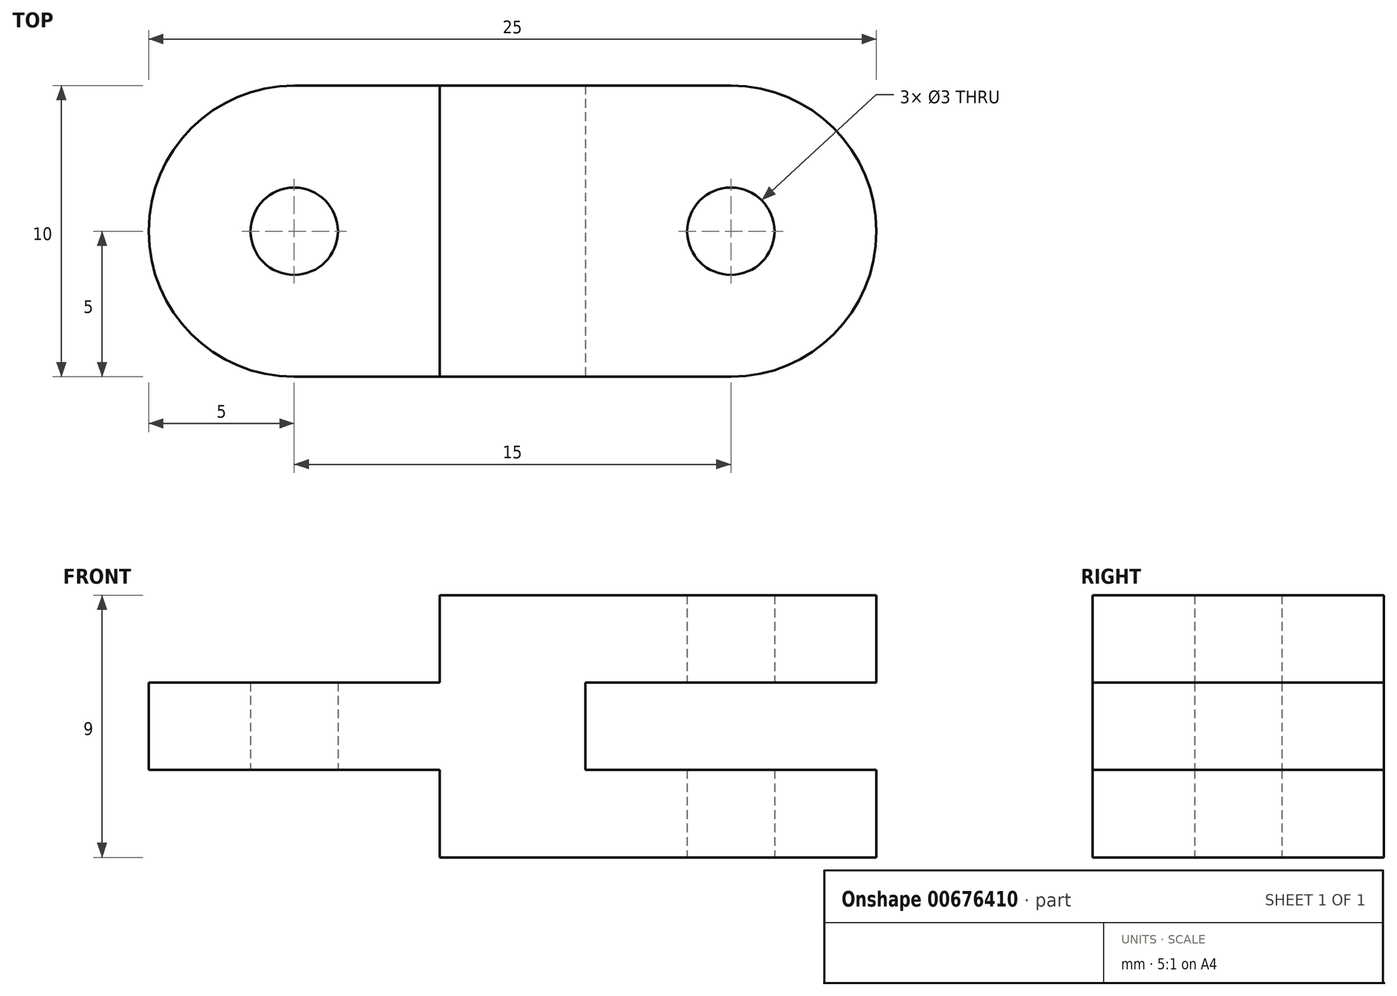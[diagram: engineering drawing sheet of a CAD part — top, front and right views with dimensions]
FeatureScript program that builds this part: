
annotation { "Feature Type Name" : "Feature", "Feature Type Description" : "" }
export const myFeature = defineFeature(function(context is Context, id is Id, definition is map)
    precondition{}
    {
        {
            var Q0;
            Q0=qCreatedBy(makeId("Top.planeOp"),FACE);
            var sketch = newSketch(context, id + "F0", { "sketchPlane" : qUnion([Q0])});
            skArc(sketch, "E0", {"start": v(-7.5, 5) * mm, "mid": v(-12.5, 0) * mm, "end": v(-7.5, -5) * mm});
            skArc(sketch, "E1", {"start": v(7.5, -5) * mm, "mid": v(12.5, 0) * mm, "end": v(7.5, 5) * mm});
            skLineSegment(sketch, "E2", {"start": v(-7.5, 5) * mm, "end": v(7.5, 5) * mm});
            skLineSegment(sketch, "E3", {"start": v(-7.5, -5) * mm, "end": v(7.5, -5) * mm});
            skCircle(sketch, "E4", {"center": v(-7.5, 0) * mm, "radius": 1.5 * mm});
            skCircle(sketch, "E5", {"center": v(7.5, 0) * mm, "radius": 1.5 * mm});
            skSolve(sketch);
        }
        {
            var Q0;
            Q0=makeQuery(id+"F0.imprint","IMPRINT",FACE,{"disambiguationData":[TD([[makeQuery(id+"F0.imprint","IMPRINT",EDGE,{"derivedFrom":sQuery(id+"F0.wireOp",EDGE,"E0")}),1.0]])]});
            extrude(context, id + "F1", {"entities" : qUnion([Q0]), "depth" : 9 * mm, "offsetDistance" : 25 * mm, "symmetric" : true});
        }
        {
            var Q0;
            Q0=makeQuery(id+"F1.opExtrude","SWEPT_FACE",FACE,{"disambiguationData":[OSD([sQuery(id+"F0.wireOp",EDGE,"E3")])]});
            var sketch = newSketch(context, id + "F2", { "sketchPlane" : qUnion([Q0])});
            skLineSegment(sketch, "E6.bottom", {"start": v(-12.5, 4.5) * mm, "end": v(-2.5, 4.5) * mm});
            skLineSegment(sketch, "E6.top", {"start": v(-12.5, 1.5) * mm, "end": v(-2.5, 1.5) * mm});
            skLineSegment(sketch, "E6.left", {"start": v(-12.5, 4.5) * mm, "end": v(-12.5, 1.5) * mm});
            skLineSegment(sketch, "E6.right", {"start": v(-2.5, 4.5) * mm, "end": v(-2.5, 1.5) * mm});
            skLineSegment(sketch, "E7.bottom", {"start": v(-12.5, -4.5) * mm, "end": v(-2.5, -4.5) * mm});
            skLineSegment(sketch, "E7.top", {"start": v(-12.5, -1.5) * mm, "end": v(-2.5, -1.5) * mm});
            skLineSegment(sketch, "E7.left", {"start": v(-12.5, -4.5) * mm, "end": v(-12.5, -1.5) * mm});
            skLineSegment(sketch, "E7.right", {"start": v(-2.5, -4.5) * mm, "end": v(-2.5, -1.5) * mm});
            skLineSegment(sketch, "E8.bottom", {"start": v(12.5, 1.5) * mm, "end": v(2.5, 1.5) * mm});
            skLineSegment(sketch, "E8.top", {"start": v(12.5, -1.5) * mm, "end": v(2.5, -1.5) * mm});
            skLineSegment(sketch, "E8.left", {"start": v(12.5, 1.5) * mm, "end": v(12.5, -1.5) * mm});
            skLineSegment(sketch, "E8.right", {"start": v(2.5, 1.5) * mm, "end": v(2.5, -1.5) * mm});
            skLineSegment(sketch, "E9", {"start": v(12.5, 4.5) * mm, "end": v(12.5, -4.5) * mm, "construction": true});
            skLineSegment(sketch, "E10", {"start": v(-12.5, -4.5) * mm, "end": v(-12.5, 4.5) * mm, "construction": true});
            skSolve(sketch);
        }
        {
            var Q0;
            {var subQ3=sQuery(id+"F2.wireOp",EDGE,"E6.left");Q0=makeQuery(id+"F2.imprint","IMPRINT",FACE,{"disambiguationData":[TD([[makeQuery(id+"F2.imprint","IMPRINT",EDGE,{"derivedFrom":subQ3}),1.0]])]});}
            var Q1;
            {var subQ4=sQuery(id+"F2.wireOp",EDGE,"E7.right");Q1=makeQuery(id+"F2.imprint","IMPRINT",FACE,{"disambiguationData":[TD([[makeQuery(id+"F2.imprint","IMPRINT",EDGE,{"derivedFrom":subQ4}),1.0]])]});}
            var Q2;
            {var subQ4=sQuery(id+"F2.wireOp",EDGE,"E6.right");Q2=makeQuery(id+"F2.imprint","IMPRINT",FACE,{"disambiguationData":[TD([[makeQuery(id+"F2.imprint","IMPRINT",EDGE,{"derivedFrom":subQ4}),-1.0]])]});}
            var Q3;
            {var subQ3=sQuery(id+"F2.wireOp",EDGE,"E7.left");Q3=makeQuery(id+"F2.imprint","IMPRINT",FACE,{"disambiguationData":[TD([[makeQuery(id+"F2.imprint","IMPRINT",EDGE,{"derivedFrom":subQ3}),-1.0]])]});}
            var Q4;
            {var subQ0=sQuery(id+"F2.wireOp",EDGE,"E8.left");Q4=makeQuery(id+"F2.imprint","IMPRINT",FACE,{"disambiguationData":[TD([[makeQuery(id+"F2.imprint","IMPRINT",EDGE,{"derivedFrom":subQ0}),-1.0]])]});}
            var Q5;
            {var subQ0=sQuery(id+"F2.wireOp",EDGE,"E8.right");Q5=makeQuery(id+"F2.imprint","IMPRINT",FACE,{"disambiguationData":[TD([[makeQuery(id+"F2.imprint","IMPRINT",EDGE,{"derivedFrom":subQ0}),1.0]])]});}
            extrude(context, id + "F3", {"entities" : qUnion([Q0, Q1, Q2, Q3, Q4, Q5]), "operationType" : NewBodyOperationType.REMOVE, "endBound" : BoundingType.THROUGH_ALL, "oppositeDirection" : true, "depth" : 25 * mm, "offsetDistance" : 25 * mm});
        }
    });
